# Revit family: INDF-FACE BASED
name_source: partatom
category: Lighting Fixtures
units: mm (PartAtom-declared; Revit-internal decimal feet)

## family parameters
Cut with Voids When Loaded = No
Host = Face
Light Source = Yes
Part Type = Normal
Room Calculation Point = No
Round Connector Dimension = Use Diameter
Shared = No

## types (12) — shared parameters
Apparent Load = 0 VA
Color Filter = 16777215
Default Elevation = 4' - 0"
Dimming Lamp Color Temperature Shift = <None>
Manufacturer = AAL
Model = INDF
Tilt Angle = 90.00°

## per-type parameters (varying)
| type | Lamp | Photometric Web File | Wattage Comments |
| INDF-RD-30LED-BW-15 | LED | INDA-RD-30LED-BW-15.IES |  |
| INDF-RD-30LED-BW-30 | LED | INDF-RD-30LED-BW-30.IES |  |
| INDF-RD-30LED-BW | LED | INDF-RD-30LED-BW.IES |  |
| INDF-RD-30LED-WW | LED | INDF-RD-30LED-WW.IES |  |
| INDF-RD-150MH-0-CDC | MH | INDF-RD-150MH-0-CDC.IES | 150 W |
| INDF-RD-150MH-15 | MH | INDF-RD-150MH-15.IES | 150 W |
| INDF-RD-150MH-30 | MH | INDF-RD-150MH-30.IES | 150 W |
| INDF-RD-150MHT6-0 CDC | MH | INDF-RD-150MHT6-0 CDC.IES | 150 W |
| INDF-RD-150MHT6-0 | MH | INDF-RD-150MHT6-0.IES | 150 W |
| INDF-RD-150MHT6-15 | MH | INDF-RD-150MHT6-15.IES | 150 W |
| INDF-RD-150MHT6-30 | MH | INDF-RD-150MHT6-30.IES | 150 W |
| INDF-RD-IL-85-0 | MH | INDF-RD-150MHT6-30.IES | 150 W |

## geometry (parser evidence)
native form markers: Sweep x2
no freeform markers — native parametric forms only
